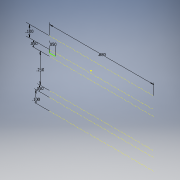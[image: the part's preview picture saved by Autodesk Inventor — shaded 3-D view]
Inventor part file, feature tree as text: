
AUTODESK INVENTOR PART (.ipt)
format: ipt  version: 2017 (Build 210142000, 142)  size: 93,696 bytes
history: native  units: in
note: dims shown in document units (in); Inventor stores cm internally (conversion verified against a paired STEP export)
features: sketch x1
ambient origin geometry x8: Origin, YZ Plane, XZ Plane, XY Plane, X Axis, Y Axis, Z Axis, Center Point
feature tree (1):
  sketch  "Sketch3"  dims[d5=0.88in d6=0.1in d7=0.05in d8=0.25in d9=0.05in d10=0.1in d11=0.05in]
